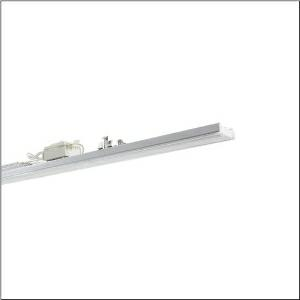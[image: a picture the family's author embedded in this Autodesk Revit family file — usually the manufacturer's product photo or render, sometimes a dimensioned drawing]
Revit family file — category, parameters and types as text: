
# Revit family: licross_r__11_recessed_mo_51tl1ede445g_b723
name_source: partatom
category: Lighting Fixtures
units: mm (PartAtom-declared; Revit-internal decimal feet)

## family parameters
Cut with Voids When Loaded = No
Host = Face
Light Source = No
Part Type = Normal
Room Calculation Point = No
Round Connector Dimension = Use Diameter
Shared = No

## types (1)
- --- (1 x LED, 4950 lm, 29.6 W, 4000K)
    Apparent Load = 30 VA
    CIE Flux Codes = 85 95 99 100 100
    Color Rendering = 80
    Color Temperature = 4000K
    Default Elevation = 1800 mm
    Description = Licross® 11 Recessed MO, luminaire insert, of sheet steel, coil coated, white, length: 750mm, width: 66mm, height: 67mm, LED rated luminous flux: 4.950lm, light colour: 840, control gear: DALI 2, with plug, 5-pole, with phase selection, mains connection: 220..240V, AC, 50/60Hz, rated input power: 30W, halogen-free wiring, primary light control with lens, of plastic, primary optical cover: cover, of PMMA, light emission: direct distribution, primary light characteristic: symmetric, protection rating (complete): IP40, insulation class (complete): insulation class I (protective earthing), certification: CE, ENEC, VDE, UKCA, protection symbol: D if used in an environment without relevant dust loads with corresponding accessories, impact resistance: IK06, permissible ambient temperature for indoor applications: -25..+35°C, corresponds to IFS (International Featured Standards) requirements for safety and quality in the food industry, reducing of maximum allowable ambient temperature of 5°C with ceiling mounting, LABS conformity tested according to VDMA 24364:2018-05, packaging unit: 1 piece
    Height = 58 mm
    Lamp = 1 x LED
    Lamp Light Flux = 4950 lm
    Lamp Power = 29.6 W
    Lamp count = 1
    Length = 750 mm
    Luminous efficacy = 167 lm/W
    Manufacturer = Siteco
    ModVariant = No
    Model = 51TL1EDE445G
    Mounting Place = Ceiling
    Mounting Type = Pendant
    Number of Poles = 1
    OnlyDefault = Yes
    Power Factor = 1
    Product Name = Licross® 11 Recessed MO
    Product group = luminaire insert
    ProductGroupID = 902
    Protection Class = Protection class I
    Protection Degree = IP 40
    RLX_Detail_Level = 1
    RLX_Emergency_Light_Flux = 0 lm
    RLX_Emergency_Type = 0
    RLX_Emergency_Type_DB = No
    RlxData = <blob elided: 29097 chars, md5=59e73ee7>
    Socket = socket
    Standby Power = 0 W
    System Light Flux = 4950 lm
    System Power = 30 W
    Type Comments = factory setting: luminous flux: 100 % | dim-lin: 254 | 378 mA
    Type Image = l_1296930.jpg
    URL = http://relux.com
    VarID = @adj_095548
    Voltage = 0 V
    Weight = 0.00 kg
    Width = 66 mm

## geometry (parser evidence)
native form markers: Blend x4, Sweep x11
no freeform markers — native parametric forms only
